# Revit family: Shower-Handshower_Kit-KOHLER-ARCHER-K-72699T_1
name_source: partatom
category: Plumbing Fixtures
revit_build: Autodesk Revit 2017 (Build: 20160225_1515(x64)
units: mm (PartAtom-declared; Revit-internal decimal feet)

## family parameters
Cut with Voids When Loaded = No
Host = Face
OmniClass Number = 23.31.17.00
OmniClass Title = Showers
Part Type = Normal
Room Calculation Point = No
Round Connector Dimension = Use Diameter
Shared = No

## types (4) — shared parameters
ADA Compliant = No
Assembly Code = D2010700
CW Connection = Yes
Cold Water Inlet = Cold Water Inlet
Date Modified = 10/09/2020
Default Elevation = 42"
Description = Wall-mounted shower faucet (150MM installation hole pitch)
Drain Included = No
Flow Rate = 3 GPM
HW Connection = Yes
Handle Clearance = 2 13/16"
Height = 36 1/2"
Hot Water Inlet = Hot Water Inlet
Length = 10 7/16"
Manufacturer = KOHLER Co.
Master Format 2014 = 22 42 23
Master Format 2014 Name = Residential Showers
Material = Premium Metal Construction
Pressure = 80.00 psi
Product Documentation Link = https://files.kohler.com.cn
Product Name = ARCHER
Product Page URL = https://www.kohler.com.cn
URL = http://www.kohler.com.cn
Vent Connection = No
Waste Connection = No
Waste Water Outlet = Waste Water Outlet
WaterSense Certified = No
Width = 8 1/8"

## per-type parameters (varying)
| type | Finish | Model | Type |
| CP- Polished Chrome | Kohler-Metal-CP-Polished_Chrome | K-72699T-B4-CP | 1 |
| AF- Flange Gold | Kohler-Metal-AF-Flange_Gold | K-72699T-B4-AF | 2 |
| BN- Roman Silver | Kohler-Metal-BN-Roman_Silver | K-72699T-B4-BN | 3 |
| 2BZ- Elegant Black | Kohler-Metal-2BZ-Elegant_Black | K-72699T-B4-2BZ | 4 |

## geometry (parser evidence)
native form markers: Sweep x6
no freeform markers — native parametric forms only
